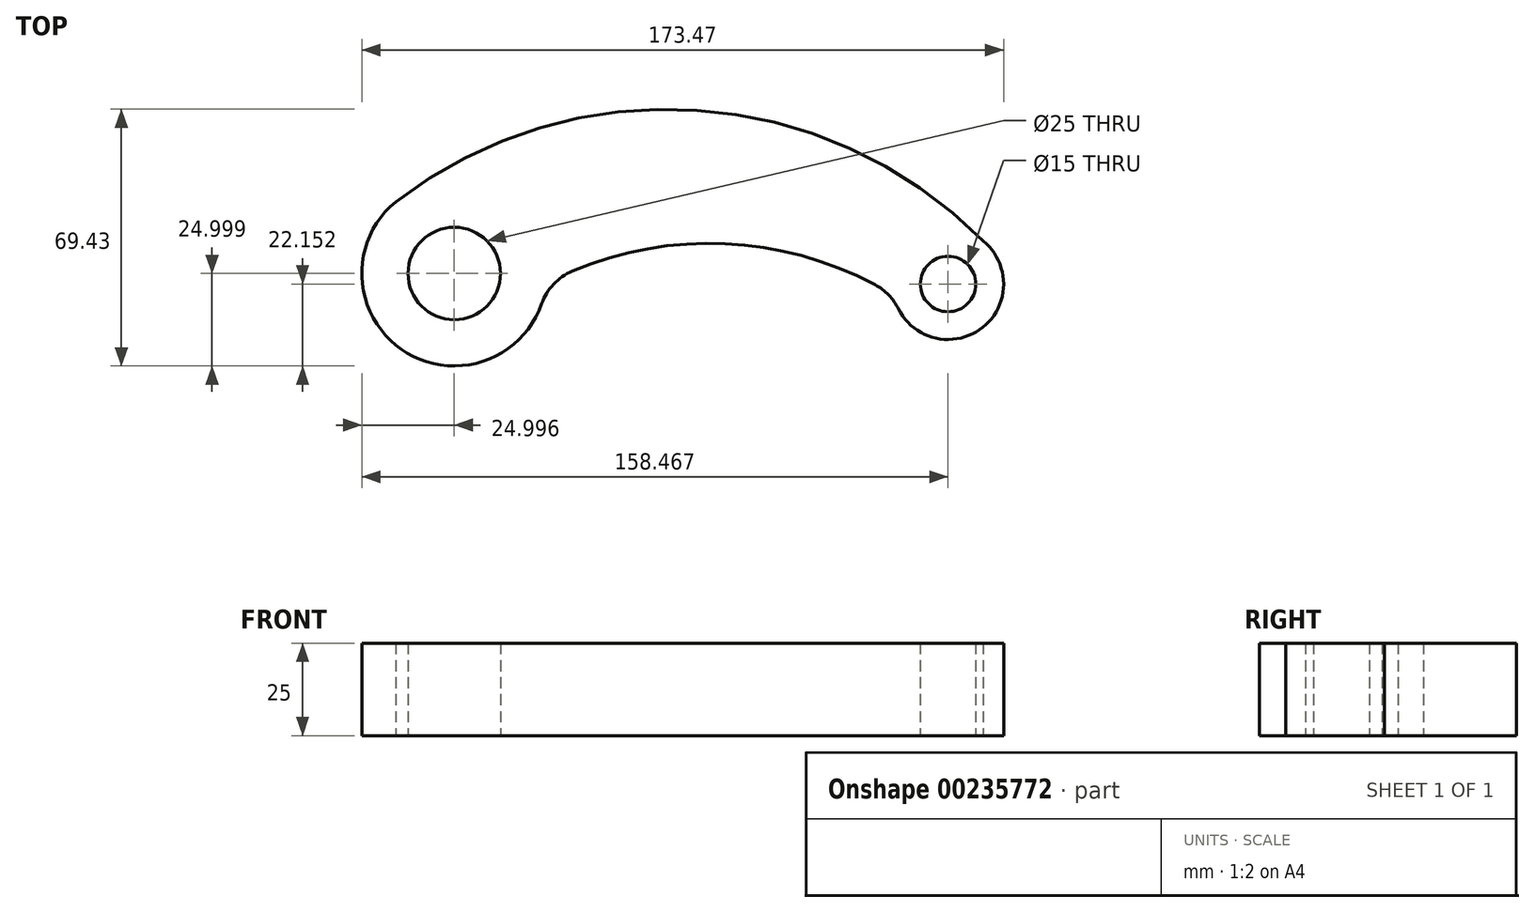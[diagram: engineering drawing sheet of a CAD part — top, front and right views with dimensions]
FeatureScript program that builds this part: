
annotation { "Feature Type Name" : "Feature", "Feature Type Description" : "" }
export const myFeature = defineFeature(function(context is Context, id is Id, definition is map)
    precondition{}
    {
        {
            var Q0;
            Q0=qCreatedBy(makeId("Top.planeOp"),FACE);
            var sketch = newSketch(context, id + "F0", { "sketchPlane" : qUnion([Q0])});
            skPoint(sketch, "E0", {"position": v(-0.1, 38.6) * mm});
            skPoint(sketch, "E1", {"position": v(-70.37, 52.6) * mm});
            skArc(sketch, "E2", {"start": v(-86.21, 71.94) * mm, "mid": v(-84.7, 32.1) * mm, "end": v(-46.76, 44.38) * mm});
            skCircle(sketch, "E3", {"center": v(-70.37, 52.6) * mm, "radius": 12.5 * mm});
            skPoint(sketch, "E4", {"position": v(63.1, 49.75) * mm});
            skArc(sketch, "E5", {"start": v(49.68, 43.04) * mm, "mid": v(72.48, 38.05) * mm, "end": v(72.57, 61.39) * mm});
            skCircle(sketch, "E6", {"center": v(63.1, 49.75) * mm, "radius": 7.5 * mm});
            skArc(sketch, "E7.trimOffspring", {"start": v(43.34, 49.55) * mm, "mid": v(2.87, 60.67) * mm, "end": v(-38.44, 53.27) * mm});
            skPoint(sketch, "E8", {"position": v(-45.37, 52.6) * mm});
            skPoint(sketch, "E9.visualSharp", {"position": v(-45.52, 49.92) * mm});
            skArc(sketch, "E9.filletArc", {"start": v(-38.44, 53.27) * mm, "mid": v(-43.54, 49.7) * mm, "end": v(-46.76, 44.38) * mm});
            skPoint(sketch, "E10.visualSharp", {"position": v(48.43, 46.63) * mm});
            skArc(sketch, "E10.filletArc", {"start": v(49.68, 43.04) * mm, "mid": v(47.02, 46.79) * mm, "end": v(43.34, 49.55) * mm});
            skPoint(sketch, "E11.start.orphan", {"position": v(77.7, 53.2) * mm});
            skPoint(sketch, "E12.end.orphan", {"position": v(55.5, 36.82) * mm});
            skPoint(sketch, "E13", {"position": v(72.57, 61.39) * mm});
            skArc(sketch, "E14", {"start": v(72.57, 61.39) * mm, "mid": v(-4.82, 96.77) * mm, "end": v(-86.21, 71.94) * mm});
            skPoint(sketch, "E15.orphan", {"position": v(-50.99, 36.82) * mm});
            skSolve(sketch);
        }
        {
            var Q0;
            Q0=makeQuery(id+"F0.imprint","IMPRINT",FACE,{"disambiguationData":[TD([[makeQuery(id+"F0.imprint","IMPRINT",EDGE,{"derivedFrom":sQuery(id+"F0.wireOp",EDGE,"E2")}),1.0]])]});
            extrude(context, id + "F1", {"entities" : qUnion([Q0]), "depth" : 25 * mm});
        }
    });
